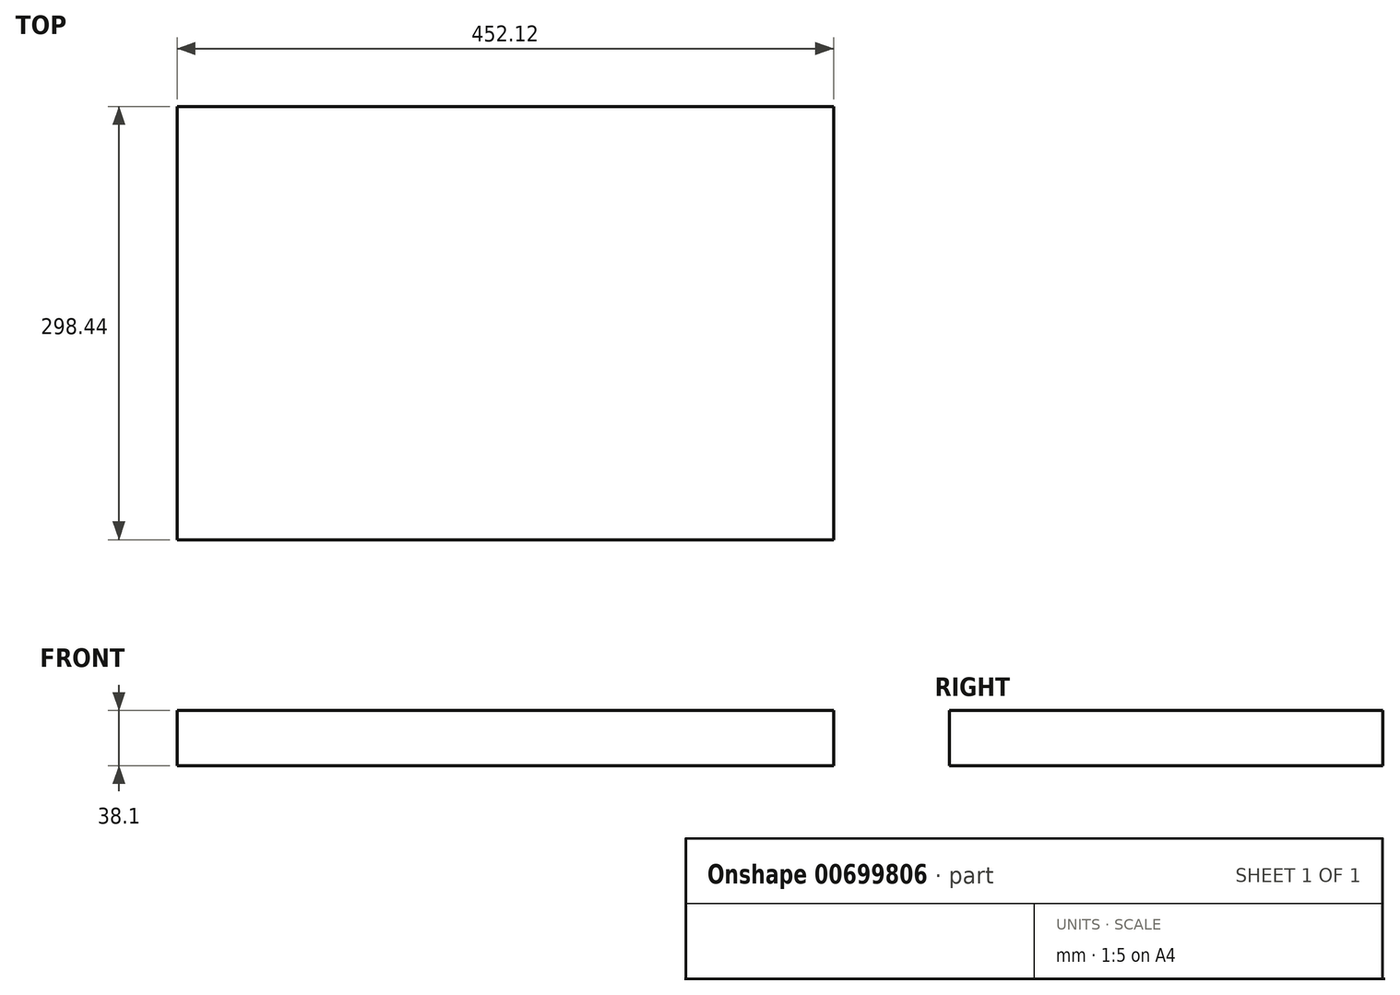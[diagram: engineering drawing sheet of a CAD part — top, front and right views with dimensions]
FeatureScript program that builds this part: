
annotation { "Feature Type Name" : "Feature", "Feature Type Description" : "" }
export const myFeature = defineFeature(function(context is Context, id is Id, definition is map)
    precondition{}
    {
        {
            var Q0;
            Q0=qCreatedBy(makeId("Top.planeOp"),FACE);
            var sketch = newSketch(context, id + "F0", { "sketchPlane" : qUnion([Q0])});
            skLineSegment(sketch, "E0.bottom", {"start": v(226.06, -149.22) * mm, "end": v(-226.06, -149.23) * mm});
            skLineSegment(sketch, "E0.top", {"start": v(226.06, 149.23) * mm, "end": v(-226.06, 149.22) * mm});
            skLineSegment(sketch, "E0.left", {"start": v(226.06, -149.22) * mm, "end": v(226.06, 149.23) * mm});
            skLineSegment(sketch, "E0.right", {"start": v(-226.06, -149.23) * mm, "end": v(-226.06, 149.22) * mm});
            skPoint(sketch, "E0.middle", {"position": v(0, 0) * mm});
            skSolve(sketch);
        }
        {
            var Q0;
            Q0=makeQuery(id+"F0.imprint","IMPRINT",FACE,{"disambiguationData":[TD([[makeQuery(id+"F0.imprint","IMPRINT",EDGE,{"derivedFrom":sQuery(id+"F0.wireOp",EDGE,"E0.bottom")}),-1.0]])]});
            extrude(context, id + "F1", {"entities" : qUnion([Q0]), "depth" : 38.1 * mm, "offsetDistance" : 25.4 * mm});
        }
    });
